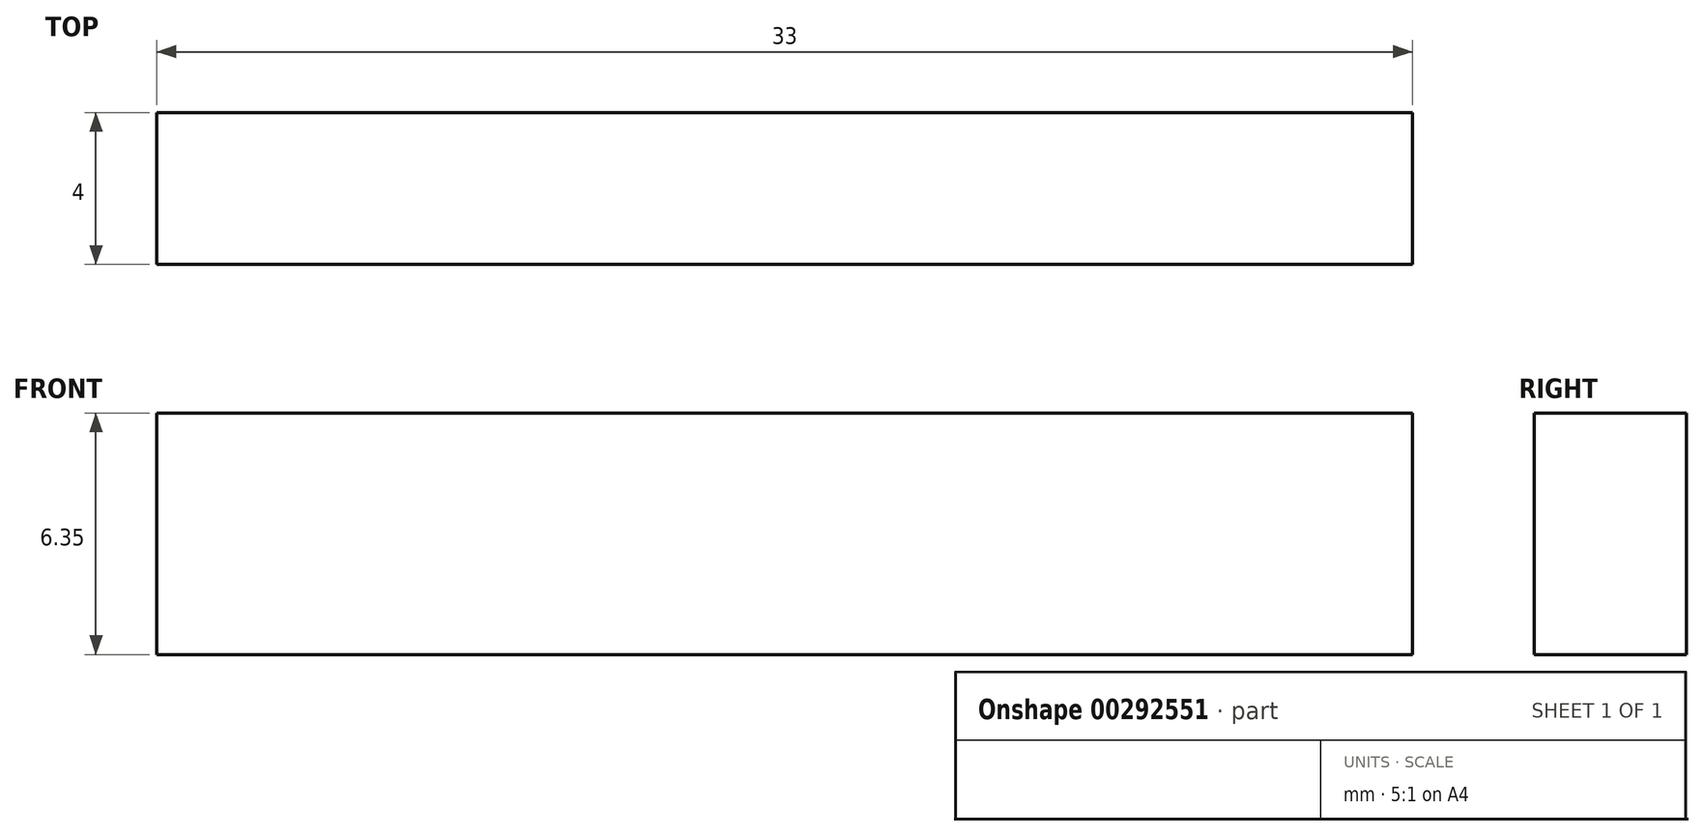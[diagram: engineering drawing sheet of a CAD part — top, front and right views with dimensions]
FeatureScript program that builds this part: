
annotation { "Feature Type Name" : "Feature", "Feature Type Description" : "" }
export const myFeature = defineFeature(function(context is Context, id is Id, definition is map)
    precondition{}
    {
        {
            var Q0;
            Q0=qCreatedBy(makeId("Front.planeOp"),FACE);
            var sketch = newSketch(context, id + "F0", { "sketchPlane" : qUnion([Q0])});
            skLineSegment(sketch, "E0.bottom", {"start": v(-16.5, 6.9) * mm, "end": v(16.5, 6.9) * mm});
            skLineSegment(sketch, "E0.top", {"start": v(-16.5, 0.55) * mm, "end": v(16.5, 0.55) * mm});
            skLineSegment(sketch, "E0.left", {"start": v(-16.5, 6.9) * mm, "end": v(-16.5, 0.55) * mm});
            skLineSegment(sketch, "E0.right", {"start": v(16.5, 6.9) * mm, "end": v(16.5, 0.55) * mm});
            skSolve(sketch);
        }
        {
            var Q0;
            Q0 = qSketchRegion(id + "F0", true);
            extrude(context, id + "F1", {"entities" : qUnion([Q0]), "depth" : 4 * mm});
        }
    });
